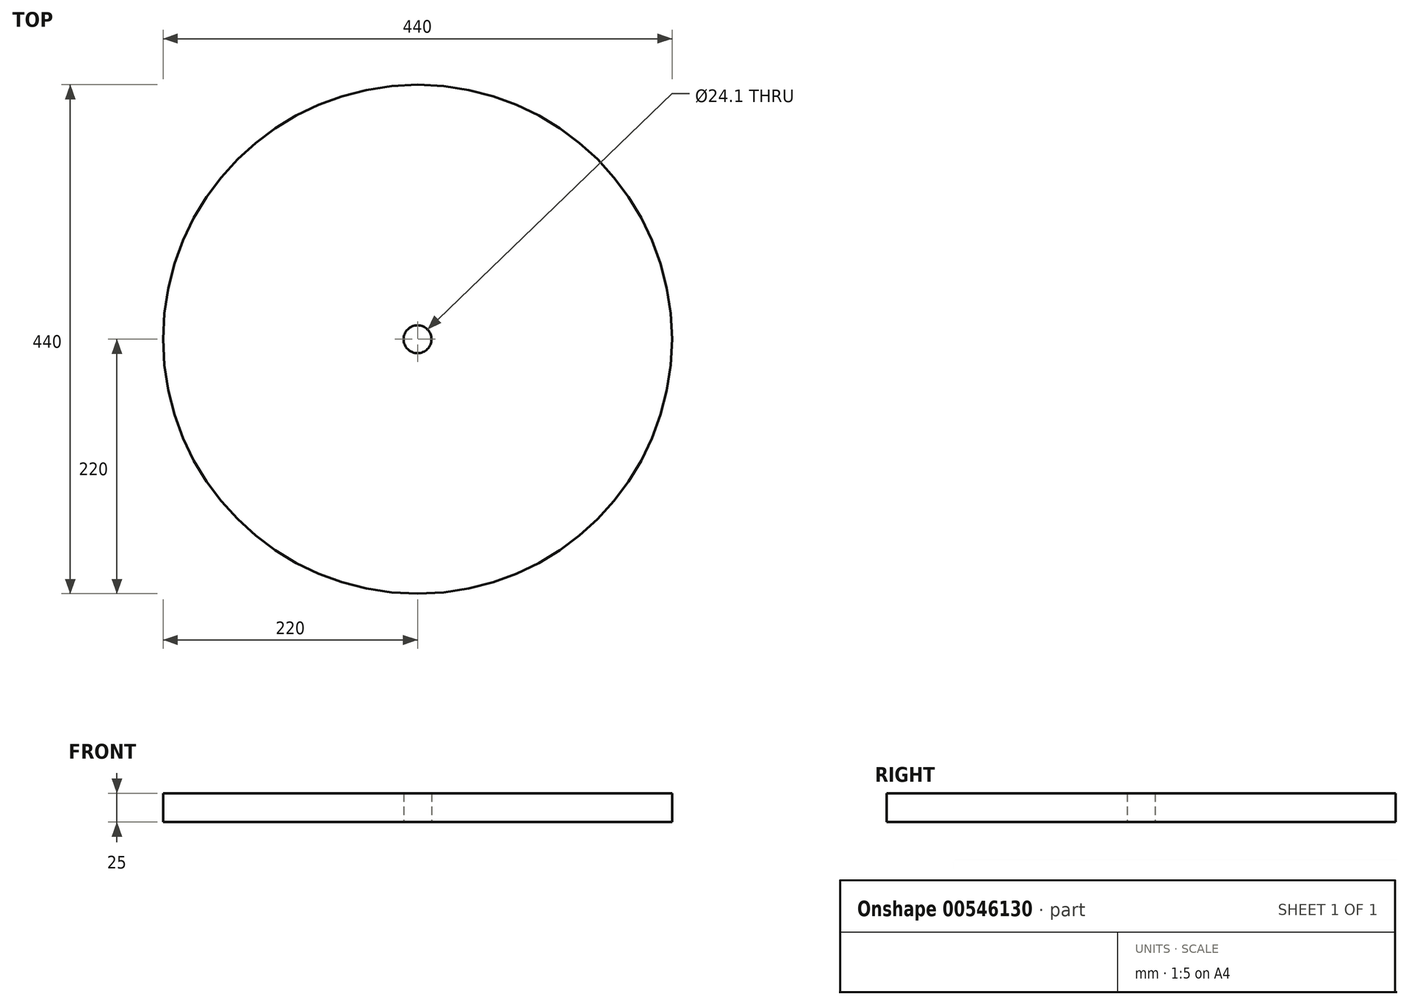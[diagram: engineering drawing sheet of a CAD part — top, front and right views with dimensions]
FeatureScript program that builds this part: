
annotation { "Feature Type Name" : "Feature", "Feature Type Description" : "" }
export const myFeature = defineFeature(function(context is Context, id is Id, definition is map)
    precondition{}
    {
        {
            var Q0;
            Q0=qCreatedBy(makeId("Top.planeOp"),FACE);
            var sketch = newSketch(context, id + "F0", { "sketchPlane" : qUnion([Q0])});
            skCircle(sketch, "E0", {"center": v(0, 0) * mm, "radius": 220 * mm});
            skCircle(sketch, "E1", {"center": v(0, 0) * mm, "radius": 12.05 * mm});
            skSolve(sketch);
        }
        {
            var Q0;
            Q0 = qSketchRegion(id + "F0", true);
            extrude(context, id + "F1", {"entities" : qUnion([Q0]), "depth" : 25 * mm, "offsetDistance" : 25 * mm});
        }
    });
